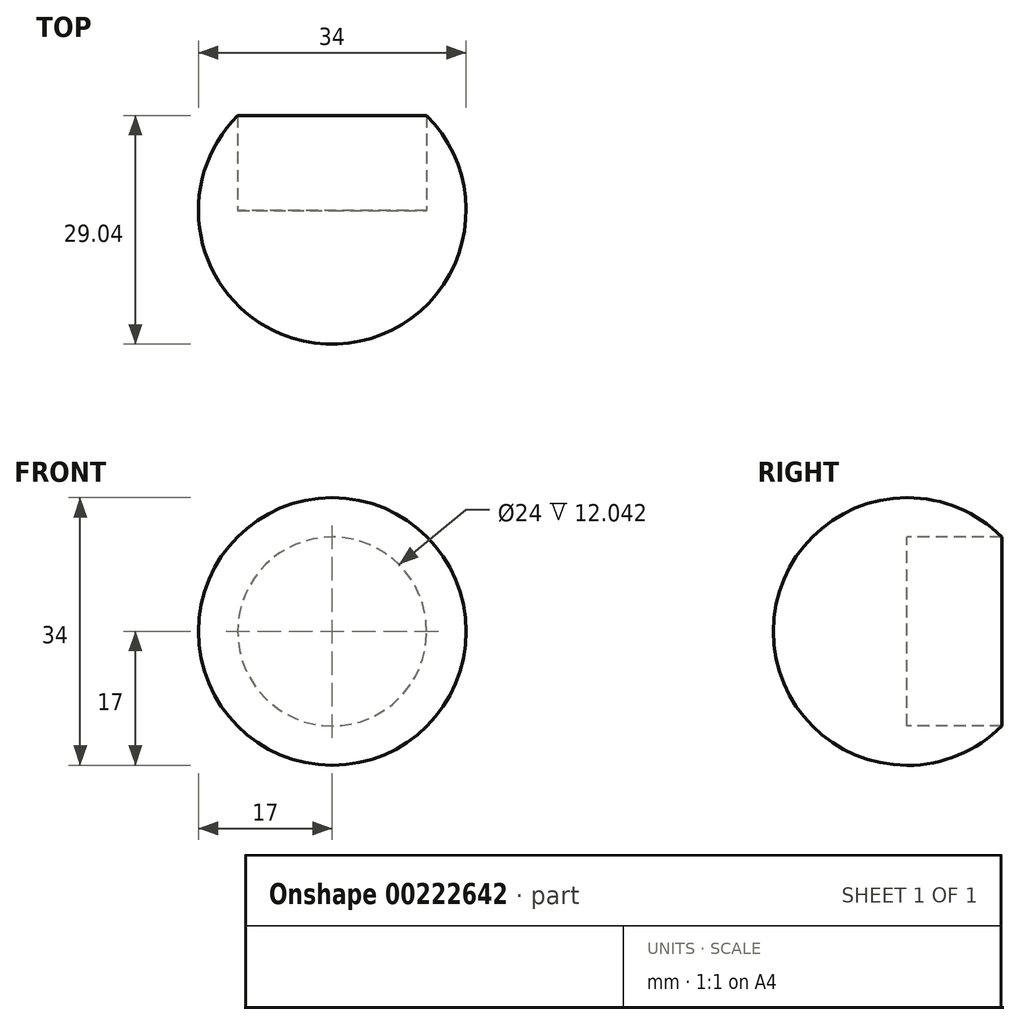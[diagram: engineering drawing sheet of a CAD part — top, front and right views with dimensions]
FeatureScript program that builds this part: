
annotation { "Feature Type Name" : "Feature", "Feature Type Description" : "" }
export const myFeature = defineFeature(function(context is Context, id is Id, definition is map)
    precondition{}
    {
        {
            var Q0;
            Q0=qCreatedBy(makeId("Front.planeOp"),FACE);
            var sketch = newSketch(context, id + "F0", { "sketchPlane" : qUnion([Q0])});
            skArc(sketch, "E0", {"start": v(0, 17) * mm, "mid": v(-17, 0) * mm, "end": v(0, -17) * mm});
            skLineSegment(sketch, "E1", {"start": v(0, 17) * mm, "end": v(0, -17) * mm});
            skSolve(sketch);
        }
        {
            var Q0;
            Q0 = qSketchRegion(id + "F0", true);
            var Q1;
            Q1=sQuery(id+"F0.wireOp",EDGE,"E1");
            revolve(context, id + "F1", {"entities" : qUnion([Q0]), "axis" : qUnion([Q1]), "revolveType" : RevolveType.FULL});
        }
        {
            var Q0;
            Q0=qCreatedBy(makeId("Front.planeOp"),FACE);
            var sketch = newSketch(context, id + "F2", { "sketchPlane" : qUnion([Q0])});
            skCircle(sketch, "E2", {"center": v(0, 0) * mm, "radius": 12 * mm});
            skSolve(sketch);
        }
        {
            var Q0;
            Q0 = qSketchRegion(id + "F2", true);
            extrude(context, id + "F3", {"entities" : qUnion([Q0]), "operationType" : NewBodyOperationType.REMOVE, "endBound" : BoundingType.THROUGH_ALL, "oppositeDirection" : true, "depth" : 25 * mm});
        }
    });
